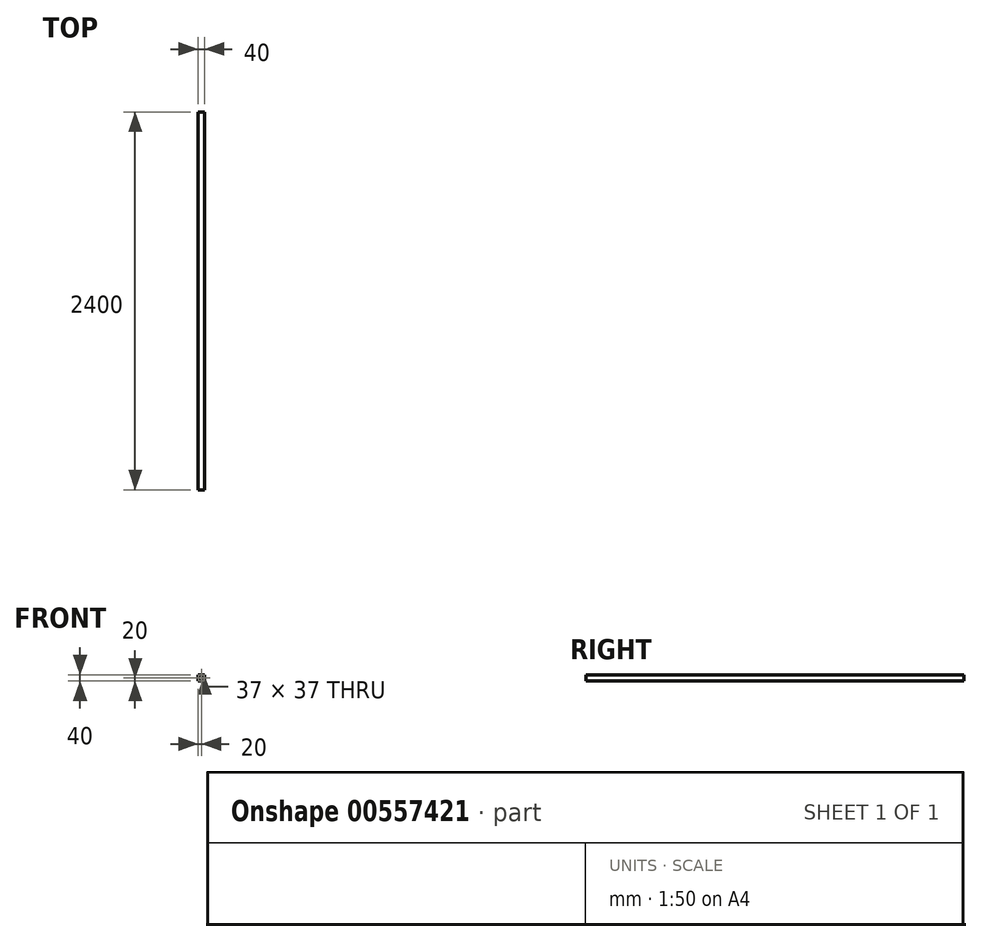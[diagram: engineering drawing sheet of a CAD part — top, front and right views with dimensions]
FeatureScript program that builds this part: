
annotation { "Feature Type Name" : "Feature", "Feature Type Description" : "" }
export const myFeature = defineFeature(function(context is Context, id is Id, definition is map)
    precondition{}
    {
        {
            var Q0;
            Q0=qCreatedBy(makeId("Front.planeOp"),FACE);
            var sketch = newSketch(context, id + "F0", { "sketchPlane" : qUnion([Q0])});
            skLineSegment(sketch, "E0.bottom", {"start": v(20, 20) * mm, "end": v(-20, 20) * mm});
            skLineSegment(sketch, "E0.top", {"start": v(20, -20) * mm, "end": v(-20, -20) * mm});
            skLineSegment(sketch, "E0.left", {"start": v(20, 20) * mm, "end": v(20, -20) * mm});
            skLineSegment(sketch, "E0.right", {"start": v(-20, 20) * mm, "end": v(-20, -20) * mm});
            skPoint(sketch, "E0.middle", {"position": v(0, 0) * mm});
            skLineSegment(sketch, "E1.0", {"start": v(-18.5, 18.5) * mm, "end": v(-18.5, -18.5) * mm});
            skLineSegment(sketch, "E1.1", {"start": v(18.5, 18.5) * mm, "end": v(-18.5, 18.5) * mm});
            skLineSegment(sketch, "E1.2", {"start": v(18.5, 18.5) * mm, "end": v(18.5, -18.5) * mm});
            skLineSegment(sketch, "E1.3", {"start": v(18.5, -18.5) * mm, "end": v(-18.5, -18.5) * mm});
            skSolve(sketch);
        }
        {
            var Q0;
            Q0=makeQuery(id+"F0.imprint","IMPRINT",FACE,{"disambiguationData":[TD([[makeQuery(id+"F0.imprint","IMPRINT",EDGE,{"derivedFrom":sQuery(id+"F0.wireOp",EDGE,"E0.bottom")}),1.0]])]});
            extrude(context, id + "F1", {"entities" : qUnion([Q0]), "endBound" : BoundingType.SYMMETRIC, "depth" : 2400 * mm, "offsetDistance" : 25 * mm});
        }
    });
